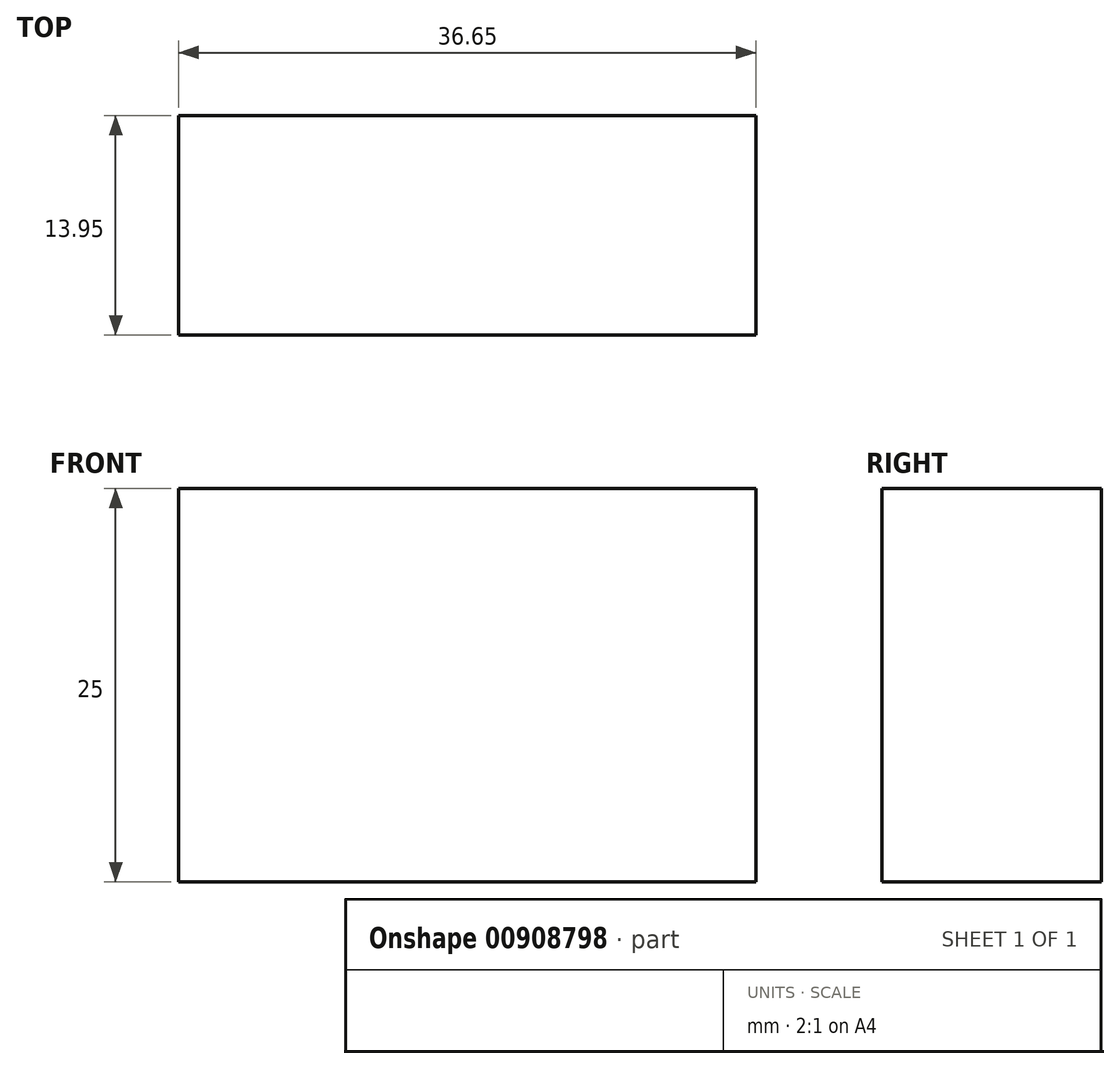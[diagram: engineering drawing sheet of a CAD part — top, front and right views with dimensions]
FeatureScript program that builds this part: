
annotation { "Feature Type Name" : "Feature", "Feature Type Description" : "" }
export const myFeature = defineFeature(function(context is Context, id is Id, definition is map)
    precondition{}
    {
        {
            var Q0;
            Q0=qCreatedBy(makeId("Top.planeOp"),FACE);
            var sketch = newSketch(context, id + "F0", { "sketchPlane" : qUnion([Q0])});
            skLineSegment(sketch, "E0.bottom", {"start": v(0, 0) * mm, "end": v(36.65, 0) * mm});
            skLineSegment(sketch, "E0.top", {"start": v(0, -13.95) * mm, "end": v(36.65, -13.95) * mm});
            skLineSegment(sketch, "E0.left", {"start": v(0, 0) * mm, "end": v(0, -13.95) * mm});
            skLineSegment(sketch, "E0.right", {"start": v(36.65, 0) * mm, "end": v(36.65, -13.95) * mm});
            skSolve(sketch);
        }
        {
            var Q0;
            Q0=makeQuery(id+"F0.imprint","IMPRINT",FACE,{"disambiguationData":[TD([[makeQuery(id+"F0.imprint","IMPRINT",EDGE,{"derivedFrom":sQuery(id+"F0.wireOp",EDGE,"E0.bottom")}),-1.0]])]});
            extrude(context, id + "F1", {"entities" : qUnion([Q0]), "depth" : 25 * mm, "offsetDistance" : 25 * mm});
        }
    });
